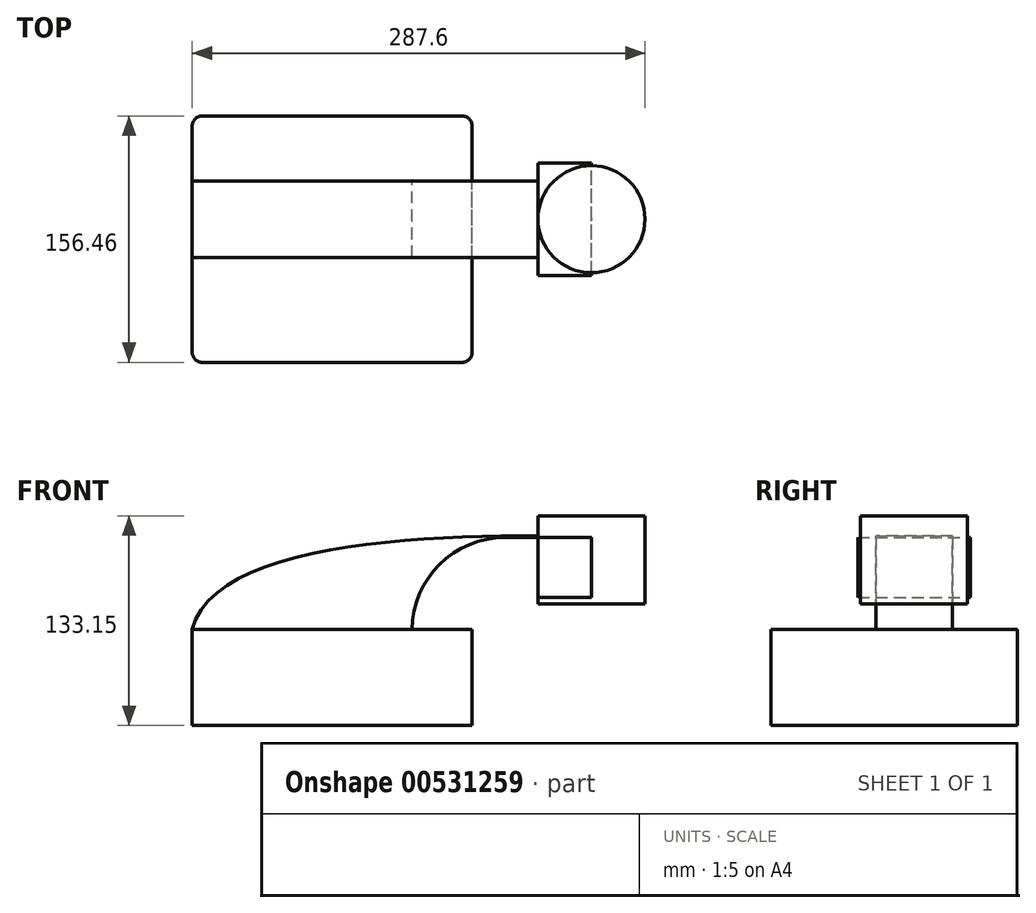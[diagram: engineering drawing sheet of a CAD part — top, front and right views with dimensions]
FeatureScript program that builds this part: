
annotation { "Feature Type Name" : "Feature", "Feature Type Description" : "" }
export const myFeature = defineFeature(function(context is Context, id is Id, definition is map)
    precondition{}
    {
        {
            var Q0;
            Q0=qCreatedBy(makeId("Front.planeOp"),FACE);
            var sketch = newSketch(context, id + "F0", { "sketchPlane" : qUnion([Q0])});
            skLineSegment(sketch, "E0.bottom", {"start": v(-88.9, 30.48) * mm, "end": v(88.9, 30.48) * mm});
            skLineSegment(sketch, "E0.top", {"start": v(-88.9, -30.48) * mm, "end": v(88.9, -30.48) * mm});
            skLineSegment(sketch, "E0.left", {"start": v(-88.9, 30.48) * mm, "end": v(-88.9, -30.48) * mm});
            skLineSegment(sketch, "E0.right", {"start": v(88.9, 30.48) * mm, "end": v(88.9, -30.48) * mm});
            skPoint(sketch, "E0.middle", {"position": v(0, 0) * mm});
            skLineSegment(sketch, "E1.bottom", {"start": v(198.7, 102.67) * mm, "end": v(130.7, 102.67) * mm});
            skLineSegment(sketch, "E1.top", {"start": v(198.7, 46.72) * mm, "end": v(130.7, 46.72) * mm});
            skLineSegment(sketch, "E1.left", {"start": v(198.7, 102.67) * mm, "end": v(198.7, 46.72) * mm});
            skLineSegment(sketch, "E1.right", {"start": v(130.7, 102.67) * mm, "end": v(130.7, 46.72) * mm});
            skPoint(sketch, "E1.middle", {"position": v(164.7, 74.7) * mm});
            skLineSegment(sketch, "E2", {"start": v(88.9, 29.9) * mm, "end": v(88.9, 30.48) * mm});
            skArc(sketch, "E3", {"start": v(88.9, 29.9) * mm, "mid": v(95.02, 44.68) * mm, "end": v(109.8, 50.8) * mm});
            skLineSegment(sketch, "E4", {"start": v(109.8, 50.8) * mm, "end": v(164.7, 50.8) * mm});
            skLineSegment(sketch, "E5", {"start": v(88.9, 30.48) * mm, "end": v(88.9, 21.63) * mm});
            skLineSegment(sketch, "E6.0", {"start": v(109.8, 88.9) * mm, "end": v(165.11, 88.9) * mm});
            skArc(sketch, "E6.1", {"start": v(50.8, 29.9) * mm, "mid": v(68.08, 71.62) * mm, "end": v(109.8, 88.9) * mm});
            skFitSpline(sketch, "E7", {"points": [v(-88.9, 30.48) * mm, v(165.11, 88.9) * mm], "startDerivative": vector(44.8, 177.19) * mm, "endDerivative": vector(259.7, -9.87) * mm});
            skLineSegment(sketch, "E8", {"start": v(164.7, 102.67) * mm, "end": v(164.7, 46.72) * mm});
            skSolve(sketch);
        }
        {
            var Q0;
            Q0=makeQuery(id+"F0.imprint","IMPRINT",FACE,{"disambiguationData":[TD([[makeQuery(id+"F0.imprint","IMPRINT",EDGE,{"derivedFrom":sQuery(id+"F0.wireOp",EDGE,"E0.top")}),1.0]])]});
            extrude(context, id + "F1", {"entities" : qUnion([Q0]), "endBound" : BoundingType.SYMMETRIC, "depth" : 25.4 * mm, "offsetDistance" : 25.4 * mm});
        }
        {
            var Q0;
            Q0=makeQuery(id+"F1.opExtrude","CAP_FACE",FACE,{"disambiguationData":[OSD([sQuery(id+"F0.wireOp",EDGE,"E0.bottom"),sQuery(id+"F0.wireOp",EDGE,"E0.top"),sQuery(id+"F0.wireOp",EDGE,"E0.left"),sQuery(id+"F0.wireOp",EDGE,"E0.right"),sQuery(id+"F0.wireOp",EDGE,"E5")])],"isStart":false});
            extrude(context, id + "F2", {"entities" : qUnion([Q0]), "operationType" : NewBodyOperationType.ADD, "endBound" : BoundingType.SYMMETRIC, "depth" : 156.46 * mm, "offsetDistance" : 25.4 * mm});
        }
        {
            var Q0;
            {var subQ1=sQuery(id+"F0.wireOp",EDGE,"E3");Q0=makeQuery(id+"F0.imprint","IMPRINT",FACE,{"disambiguationData":[TD([[makeQuery(id+"F0.imprint","IMPRINT",EDGE,{"derivedFrom":subQ1}),1.0]])]});}
            var Q1;
            {var subQ0=sQuery(id+"F0.wireOp",EDGE,"E4");var subQ1=sQuery(id+"F0.wireOp",EDGE,"E1.right");var subQ2=makeQuery(id+"F0.imprint","INTERSECT",VERTEX,{"derivedFrom":[subQ1,subQ0]});Q1=makeQuery(id+"F0.imprint","IMPRINT",FACE,{"disambiguationData":[TD([[makeQuery(id+"F0.imprint","IMPRINT",EDGE,{"disambiguationData":[TD([[subQ2,1.0]])],"derivedFrom":subQ1}),1.0]])]});}
            extrude(context, id + "F3", {"entities" : qUnion([Q0, Q1]), "operationType" : NewBodyOperationType.ADD, "endBound" : BoundingType.SYMMETRIC, "depth" : 71.63 * mm, "offsetDistance" : 25.4 * mm});
        }
        {
            var Q0;
            {var subQ5=sQuery(id+"F0.wireOp",EDGE,"E7");var subQ6=sQuery(id+"F0.wireOp",EDGE,"E1.right");var subQ7=makeQuery(id+"F0.imprint","INTERSECT",VERTEX,{"derivedFrom":[subQ6,subQ5]});Q0=makeQuery(id+"F0.imprint","IMPRINT",FACE,{"disambiguationData":[TD([[makeQuery(id+"F0.imprint","IMPRINT",EDGE,{"disambiguationData":[TD([[subQ7,-1.0]])],"derivedFrom":subQ6}),-1.0]])]});}
            extrude(context, id + "F4", {"entities" : qUnion([Q0]), "endBound" : BoundingType.SYMMETRIC, "depth" : 48.77 * mm, "offsetDistance" : 25.4 * mm});
        }
        {
            var Q0;
            {var subQ5=sQuery(id+"F0.wireOp",EDGE,"E1.left");Q0=makeQuery(id+"F0.imprint","IMPRINT",FACE,{"disambiguationData":[TD([[makeQuery(id+"F0.imprint","IMPRINT",EDGE,{"derivedFrom":subQ5}),-1.0]])]});}
            var Q1;
            Q1=sQuery(id+"F0.wireOp",EDGE,"E8");
            revolve(context, id + "F5", {"entities" : qUnion([Q0]), "axis" : qUnion([Q1]), "revolveType" : RevolveType.FULL});
        }
        {
            var Q0;
            Q0=makeQuery(id+"F2.opExtrude","CAP_EDGE",EDGE,{"disambiguationData":[OSD([sQuery(id+"F0.wireOp",EDGE,"E0.left")])],"isStart":false});
            var Q1;
            Q1=makeQuery(id+"F2.opExtrude","CAP_EDGE",EDGE,{"disambiguationData":[OSD([sQuery(id+"F0.wireOp",EDGE,"E0.right"),sQuery(id+"F0.wireOp",EDGE,"E5")])],"isStart":false});
            var Q2;
            Q2=makeQuery(id+"F2.opExtrude","CAP_EDGE",EDGE,{"disambiguationData":[OSD([sQuery(id+"F0.wireOp",EDGE,"E0.left")])],"isStart":true});
            var Q3;
            Q3=makeQuery(id+"F2.opExtrude","CAP_EDGE",EDGE,{"disambiguationData":[OSD([sQuery(id+"F0.wireOp",EDGE,"E0.right"),sQuery(id+"F0.wireOp",EDGE,"E5")])],"isStart":true});
            fillet(context, id + "F6", {"entities" : qUnion([Q0, Q1, Q2, Q3]), "radius" : 6.35 * mm, "tangentPropagation" : true, "allowEdgeOverflow" : false});
        }
    });
